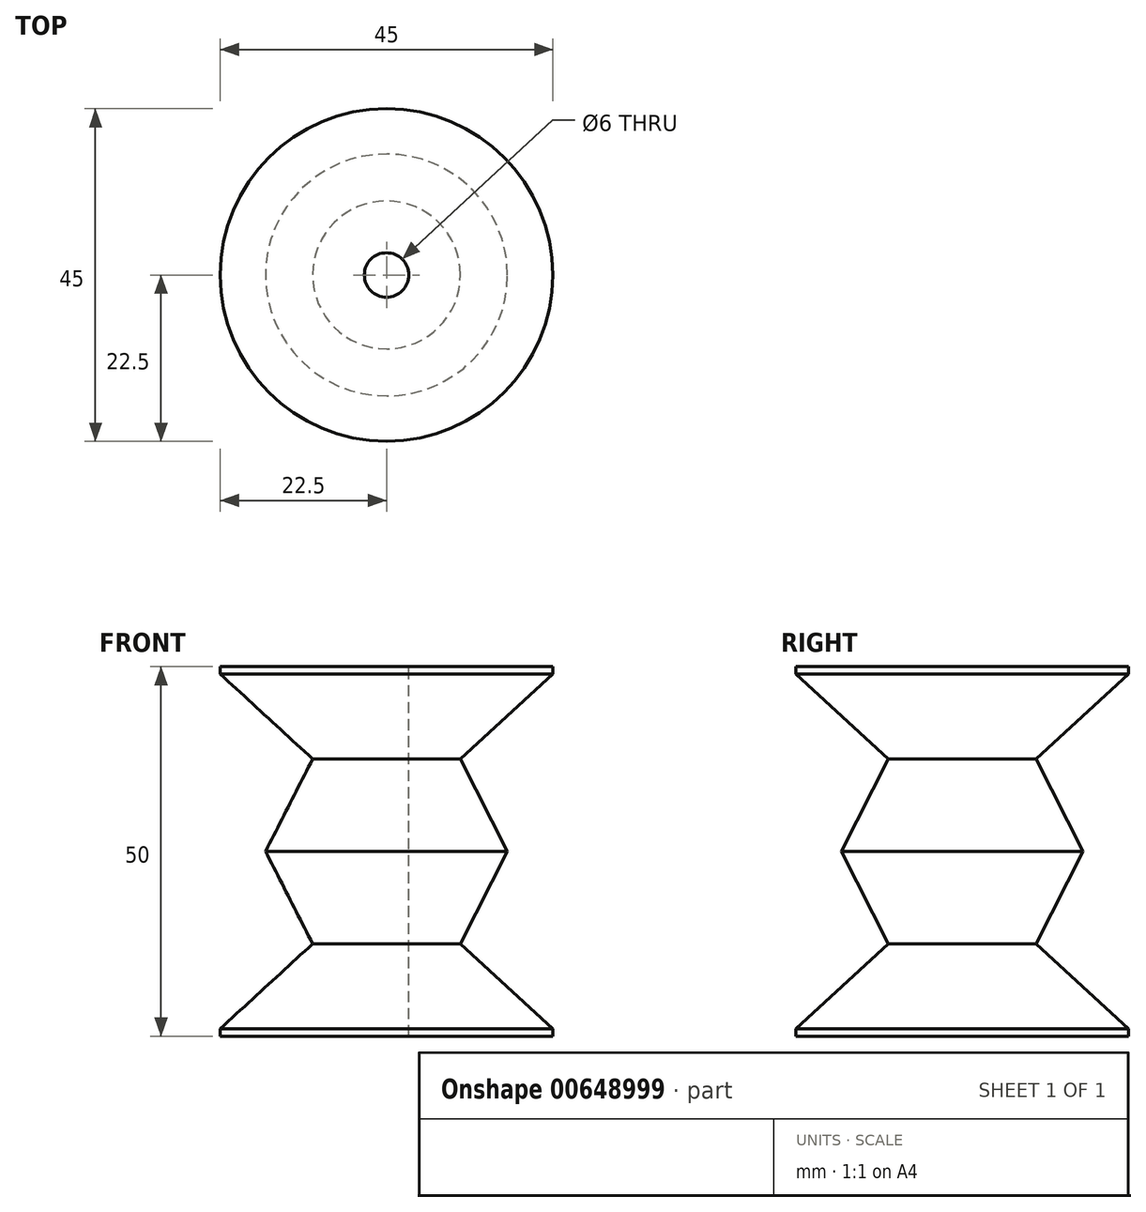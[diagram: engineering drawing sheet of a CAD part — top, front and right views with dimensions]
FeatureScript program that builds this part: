
annotation { "Feature Type Name" : "Feature", "Feature Type Description" : "" }
export const myFeature = defineFeature(function(context is Context, id is Id, definition is map)
    precondition{}
    {
        {
            var Q0;
            Q0=qCreatedBy(makeId("Front.planeOp"),FACE);
            var sketch = newSketch(context, id + "F0", { "sketchPlane" : qUnion([Q0])});
            skLineSegment(sketch, "E0", {"start": v(0, 0) * mm, "end": v(22.5, 0) * mm});
            skLineSegment(sketch, "E1", {"start": v(0, 0) * mm, "end": v(0, 50) * mm});
            skLineSegment(sketch, "E2", {"start": v(0, 50) * mm, "end": v(22.5, 50) * mm});
            skLineSegment(sketch, "E3", {"start": v(22.5, 25) * mm, "end": v(22.5, 25) * mm});
            skLineSegment(sketch, "E4", {"start": v(22.5, 50) * mm, "end": v(22.5, 49) * mm});
            skLineSegment(sketch, "E5", {"start": v(22.5, 0) * mm, "end": v(22.5, 1) * mm});
            skLineSegment(sketch, "E6", {"start": v(0, 0) * mm, "end": v(0, 25) * mm});
            skLineSegment(sketch, "E7", {"start": v(0, 12.5) * mm, "end": v(10, 12.5) * mm});
            skLineSegment(sketch, "E8", {"start": v(10, 12.5) * mm, "end": v(22.5, 1) * mm});
            skLineSegment(sketch, "E9.MirrorCS", {"start": v(0, 37.5) * mm, "end": v(10, 37.5) * mm});
            skLineSegment(sketch, "E10.MirrorCS", {"start": v(10, 37.5) * mm, "end": v(22.5, 49) * mm});
            skLineSegment(sketch, "E11", {"start": v(0, 25) * mm, "end": v(16.37, 25) * mm});
            skLineSegment(sketch, "E12", {"start": v(10, 37.5) * mm, "end": v(16.37, 25) * mm});
            skLineSegment(sketch, "E13", {"start": v(10, 12.5) * mm, "end": v(16.37, 25) * mm});
            skSolve(sketch);
        }
        {
            var Q0;
            Q0 = qSketchRegion(id + "F0", true);
            var Q1;
            Q1=sQuery(id+"F0.wireOp",EDGE,"E1");
            revolve(context, id + "F1", {"entities" : qUnion([Q0]), "axis" : qUnion([Q1]), "revolveType" : RevolveType.FULL});
        }
        {
            var Q0;
            Q0=makeQuery(id+"F1.opRevolve","SWEPT_FACE",FACE,{"disambiguationData":[OSD([sQuery(id+"F0.wireOp",EDGE,"E2")])]});
            var sketch = newSketch(context, id + "F2", { "sketchPlane" : qUnion([Q0])});
            skCircle(sketch, "E14", {"center": v(0, 0) * mm, "radius": 3 * mm});
            skSolve(sketch);
        }
        {
            var Q0;
            Q0 = qSketchRegion(id + "F2", true);
            extrude(context, id + "F3", {"entities" : qUnion([Q0]), "operationType" : NewBodyOperationType.REMOVE, "oppositeDirection" : true, "depth" : 50 * mm, "offsetDistance" : 25 * mm});
        }
    });
